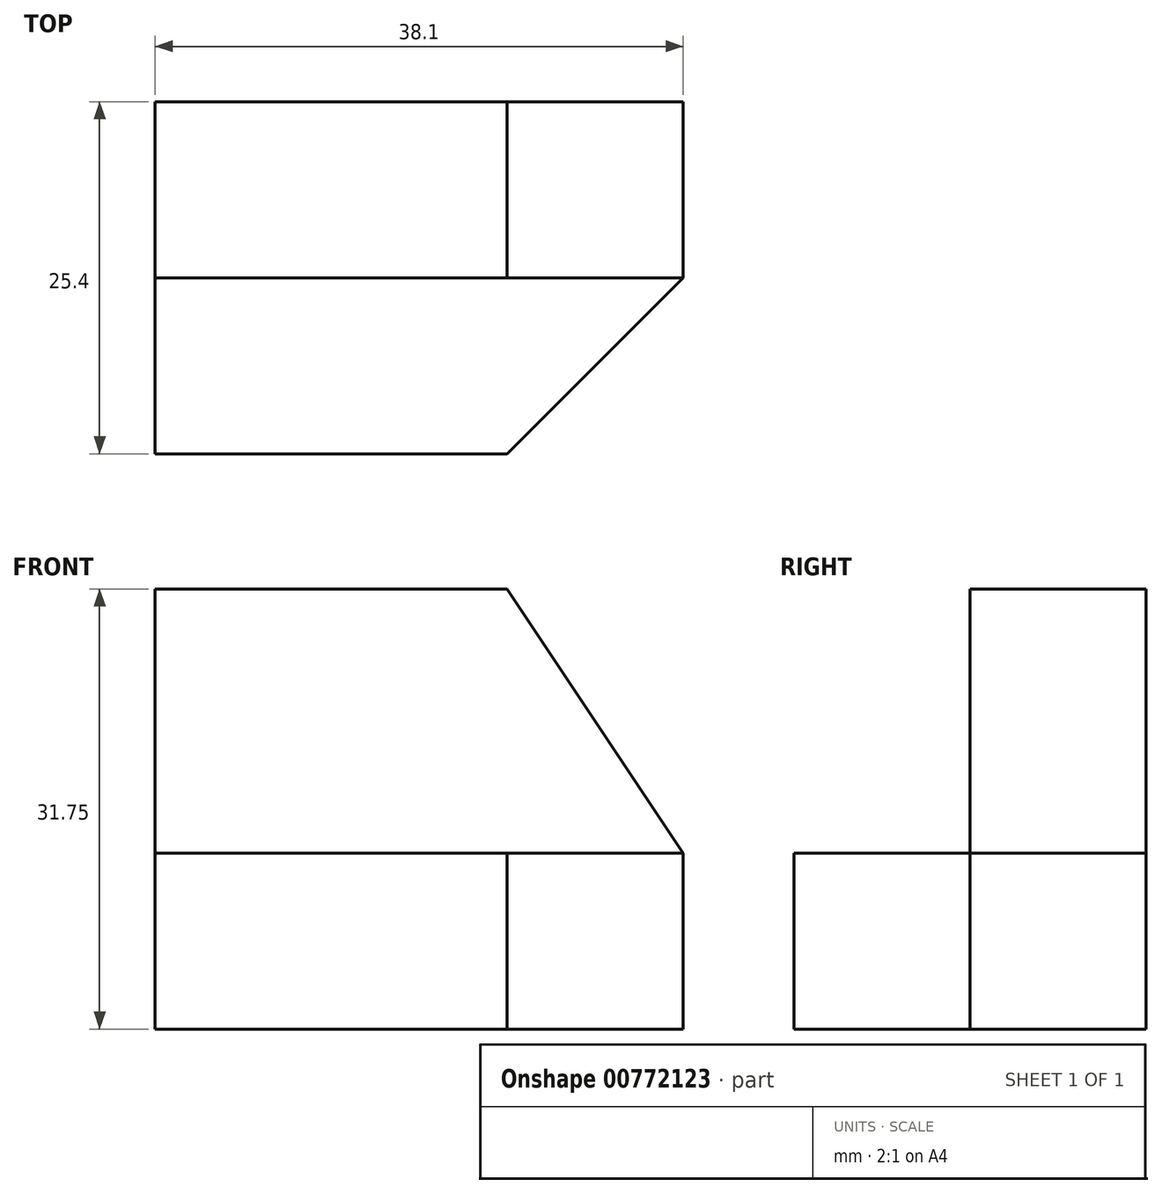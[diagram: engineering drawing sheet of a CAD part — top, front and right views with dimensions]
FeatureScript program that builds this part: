
annotation { "Feature Type Name" : "Feature", "Feature Type Description" : "" }
export const myFeature = defineFeature(function(context is Context, id is Id, definition is map)
    precondition{}
    {
        {
            var Q0;
            Q0=qCreatedBy(makeId("Front.planeOp"),FACE);
            var sketch = newSketch(context, id + "F0", { "sketchPlane" : qUnion([Q0])});
            skLineSegment(sketch, "E0", {"start": v(0, 0) * mm, "end": v(38.1, 0) * mm});
            skLineSegment(sketch, "E1", {"start": v(38.1, 0) * mm, "end": v(38.1, 31.75) * mm});
            skLineSegment(sketch, "E2", {"start": v(38.1, 31.75) * mm, "end": v(0, 31.75) * mm});
            skLineSegment(sketch, "E3", {"start": v(0, 31.75) * mm, "end": v(0, 0) * mm});
            skSolve(sketch);
        }
        {
            var Q0;
            Q0 = qSketchRegion(id + "F0", true);
            extrude(context, id + "F1", {"entities" : qUnion([Q0]), "depth" : 25.4 * mm, "offsetDistance" : 25.4 * mm});
        }
        {
            var Q0;
            Q0=makeQuery(id+"F1.opExtrude","SWEPT_FACE",FACE,{"disambiguationData":[OSD([sQuery(id+"F0.wireOp",EDGE,"E1")])]});
            var sketch = newSketch(context, id + "F2", { "sketchPlane" : qUnion([Q0])});
            skLineSegment(sketch, "E4", {"start": v(-25.4, 0) * mm, "end": v(-25.4, 12.7) * mm});
            skLineSegment(sketch, "E5", {"start": v(-25.4, 12.7) * mm, "end": v(-12.7, 12.7) * mm});
            skLineSegment(sketch, "E6", {"start": v(-12.7, 12.7) * mm, "end": v(-12.7, 31.75) * mm});
            skSolve(sketch);
        }
        {
            var Q0;
            {var subQ0=sQuery(id+"F2.wireOp",EDGE,"E5");Q0=makeQuery(id+"F2.imprint","IMPRINT",FACE,{"disambiguationData":[TD([[makeQuery(id+"F2.imprint","IMPRINT",EDGE,{"derivedFrom":subQ0}),1.0]])]});}
            extrude(context, id + "F3", {"entities" : qUnion([Q0]), "operationType" : NewBodyOperationType.REMOVE, "oppositeDirection" : true, "depth" : 38.1 * mm, "offsetDistance" : 25.4 * mm});
        }
        {
            var Q0;
            Q0=makeQuery(id+"F3.boolean.opBoolean","COPY",FACE,{"derivedFrom":makeQuery(id+"F3.opExtrude","SWEPT_FACE",FACE,{"disambiguationData":[OSD([sQuery(id+"F2.wireOp",EDGE,"E5")])]})});
            var sketch = newSketch(context, id + "F4", { "sketchPlane" : qUnion([Q0])});
            skLineSegment(sketch, "E7", {"start": v(0, -25.4) * mm, "end": v(25.4, -25.4) * mm});
            skLineSegment(sketch, "E8", {"start": v(25.4, -25.4) * mm, "end": v(38.1, -12.7) * mm});
            skSolve(sketch);
        }
        {
            var Q0;
            {var subQ0=sQuery(id+"F4.wireOp",EDGE,"E8");Q0=makeQuery(id+"F4.imprint","IMPRINT",FACE,{"disambiguationData":[TD([[makeQuery(id+"F4.imprint","IMPRINT",EDGE,{"derivedFrom":subQ0}),-1.0]])]});}
            extrude(context, id + "F5", {"entities" : qUnion([Q0]), "operationType" : NewBodyOperationType.REMOVE, "oppositeDirection" : true, "depth" : 12.7 * mm, "offsetDistance" : 25.4 * mm});
        }
        {
            var Q0;
            Q0=makeQuery(id+"F3.boolean.opBoolean","COPY",FACE,{"derivedFrom":makeQuery(id+"F3.opExtrude","SWEPT_FACE",FACE,{"disambiguationData":[OSD([sQuery(id+"F2.wireOp",EDGE,"E6")])]})});
            var sketch = newSketch(context, id + "F6", { "sketchPlane" : qUnion([Q0])});
            skLineSegment(sketch, "E9", {"start": v(0, 31.75) * mm, "end": v(25.4, 31.75) * mm});
            skLineSegment(sketch, "E10", {"start": v(25.4, 31.75) * mm, "end": v(38.1, 12.7) * mm});
            skSolve(sketch);
        }
        {
            var Q0;
            {var subQ0=sQuery(id+"F6.wireOp",EDGE,"E10");Q0=makeQuery(id+"F6.imprint","IMPRINT",FACE,{"disambiguationData":[TD([[makeQuery(id+"F6.imprint","IMPRINT",EDGE,{"derivedFrom":subQ0}),1.0]])]});}
            extrude(context, id + "F7", {"entities" : qUnion([Q0]), "operationType" : NewBodyOperationType.REMOVE, "oppositeDirection" : true, "depth" : 12.7 * mm, "offsetDistance" : 25.4 * mm});
        }
    });
